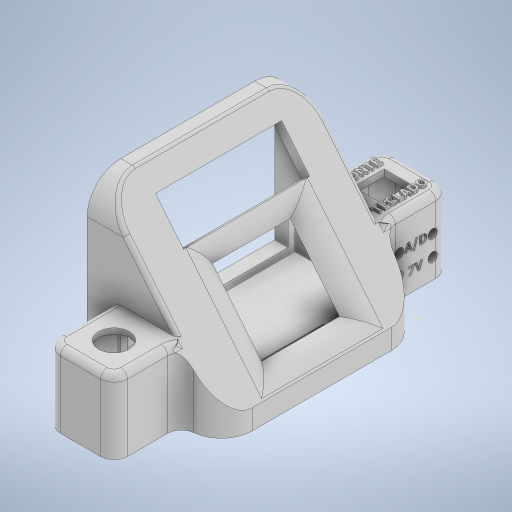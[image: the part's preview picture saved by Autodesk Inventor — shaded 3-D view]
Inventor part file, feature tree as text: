
AUTODESK INVENTOR PART (.ipt)
format: ipt  version: 2024.1 (Build 281209000, 209)  size: 1,036,800 bytes
history: native  units: mm
features: sketch x26, extrude x24, fillet x8, other x2
ambient origin geometry x8: Origin, YZ Plane, XZ Plane, XY Plane, X Axis, Y Axis, Z Axis, Center Point
bodies: Body1 (feature_tree)
feature tree (60):
  other  "Sólido1"
  extrude  "Extrusão1"  Depth=150.0mm
  extrude  "Extrusão2"  Depth=10.0mm
  extrude  "Extrusão27"  Depth=5.0mm
  extrude  "Extrusão28"  Depth=10.0mm TaperAngle=0.0deg
  extrude  "Extrusão29"  Depth=76.0mm
  sketch  "Esboço37"  dims[d175=10.0mm d176=33.0mm]
  extrude  "Extrusão30"  Depth=10.0mm
  extrude  "Extrusão31"  Depth=96.0mm
  extrude  "Extrusão32"  Depth=2.0mm
  extrude  "Extrusão33"  Depth=25.0mm
  extrude  "Extrusão34"  Depth=25.0mm
  extrude  "Extrusão35"  Depth=10.0mm
  extrude  "Extrusão36"  Depth=10.0mm
  extrude  "Extrusão37"  Depth=10.0mm TaperAngle=0.0deg
  extrude  "Extrusão38"  Depth=80.0mm
  extrude  "Extrusão39"  Depth=10.0mm TaperAngle=0.0deg
  extrude  "Extrusão40"  Depth=10.0mm
  fillet  "Arredondamento8"  Radius=10.0mm
  extrude  "Extrusão41"  Depth=10.0mm
  extrude  "Extrusão42"  Depth=10.0mm
  fillet  "Arredondamento9"  Radius=10.0mm
  extrude  "Extrusão43"  Depth=30.0mm
  fillet  "Arredondamento10"  Radius=50.0mm
  fillet  "Arredondamento11"  Radius=50.0mm
  fillet  "Arredondamento12"  Radius=50.0mm
  extrude  "Extrusão44"  Depth=23.0mm
  fillet  "Arredondamento13"  Radius=50.0mm
  fillet  "Arredondamento14"  Radius=5.0mm
  extrude  "Extrusão45"  Depth=5.0mm
  extrude  "Extrusão46"  Depth=46.0mm TaperAngle=0.0deg
  extrude  "Extrusão47"  Depth=5.0mm
  sketch  "Esboço56"  dims[d231=10.0mm d232=0.0mm]
  extrude  "Extrusão48"  Depth=5.0mm
  fillet  "Arredondamento15"  Radius=45.0mm
  sketch  "Esboço1"  dims[d0=100.0mm d1=150.0mm]
  sketch  "Esboço2"  dims[d2=10.0mm d3=0.0mm d4=110.0mm]
  sketch  "Esboço34"  dims[d5=15.0mm d6=5.0mm]
  sketch  "Esboço35"  dims[d7=10.0mm d8=150.0mm d9=0.0mm]
  sketch  "Esboço36"  dims[d173=5.0mm d174=76.0mm]
  sketch  "Esboço38"  dims[d177=46.5mm d178=96.0mm]
  sketch  "Esboço39"  dims[d179=33.0mm d180=2.0mm]
  sketch  "Esboço40"  dims[d181=12.5mm d182=25.0mm]
  sketch  "Esboço41"  dims[d183=5.0mm d184=25.0mm]
  sketch  "Esboço42"  dims[d185=10.0mm d186=0.0mm d187=10.0mm]
  sketch  "Esboço43"  dims[d188=10.0mm d189=10.0mm]
  sketch  "Esboço44"  dims[d190=10.0mm d191=10.0mm d192=0.0mm]
  sketch  "Esboço45"  dims[d193=5.0mm d194=80.0mm]
  sketch  "Esboço46"  dims[d195=10.0mm d196=0.0mm d197=5.0mm d198=0.0mm]
  sketch  "Esboço47"  dims[d199=5.0mm d200=0.0mm d201=20.0mm d202=10.0mm]
  sketch  "Esboço48"  dims[d203=40.0mm d204=10.0mm]
  sketch  "Esboço49"  dims[d205=50.0mm d206=40.0mm d207=10.0mm]
  sketch  "Esboço50"  dims[d208=50.0mm d209=0.0mm d210=30.0mm d211=50.0mm d212=50.0mm d213=50.0mm]
  sketch  "Esboço51"  dims[d214=50.0mm d215=0.0mm d216=23.0mm d217=50.0mm d218=0.0mm d219=5.0mm]
  sketch  "Esboço52"  dims[d220=5.0mm d221=5.0mm]
  sketch  "Esboço53"  dims[d222=5.0mm d223=46.0mm d224=0.0mm]
  other  "Contorno projetado2"
  sketch  "Esboço54"  dims[d225=5.0mm d226=5.0mm]
  sketch  "Esboço55"  dims[d227=5.0mm d228=5.0mm d229=45.0mm d230=0.0mm]
  sketch  "Esboço57"  dims[d233=10.0mm d234=0.0mm d235=10.0mm d236=20.0mm d237=11.5mm d238=23.0mm d239=10.0mm d240=0.0mm d241=25.0mm d242=25.0mm d243=15.0mm d244=12.5mm d245=25.0mm d246=7.0mm d247=7.0mm d248=7.0mm d249=7.0mm d250=5.0mm d251=0.0mm d252=4.0mm d253=45.0mm d254=28.0mm d255=56.0mm d256=26.0mm d257=3.0mm d258=58.0mm d259=58.0mm d260=58.0mm d261=58.0mm d262=10.0mm d263=0.0mm d264=10.0mm d265=0.0mm d266=21.0mm d267=1.0mm d268=1.0mm d269=35.0mm d270=10.0mm d271=0.0mm d272=25.0mm d273=23.0mm d274=10.0mm d275=3.0mm d276=3.0mm d277=3.0mm d278=10.0mm d279=0.0mm d280=10.0mm d281=5.0mm d282=5.0mm d283=0.0mm d284=2.0mm d285=0.0mm d286=2.0mm d287=0.0mm d288=5.0mm d289=0.0mm d290=3.0mm d10=0.5mm d11=0.872665mm]
